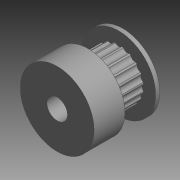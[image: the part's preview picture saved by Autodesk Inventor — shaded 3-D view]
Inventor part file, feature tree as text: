
AUTODESK INVENTOR PART (.ipt)
format: ipt  version: 2015 SP1 (Build 190203100, 203)  size: 155,648 bytes
history: native  units: mm
features: sketch x2, revolve x1, extrude x1, pattern_circular x1
ambient origin geometry x8: Origin, YZ Plane, XZ Plane, XY Plane, X Axis, Y Axis, Z Axis, Center Point
bodies: Solid1 (feature_tree)
feature tree (5):
  revolve  "Revolution1"  [1 undecoded]
  extrude  "Extrusion1"  Depth=9.0mm
  pattern_circular  "Circular Pattern1"  [2 undecoded]
  sketch  "Sketch1"  dims[d0=2.5mm d1=7.5mm]
  sketch  "Sketch2"  dims[d2=7.5mm d3=9.0mm d4=1.0mm d6=6.1mm d7=90.0deg d8=2.0mm d9=6.7mm d10=10.0mm d11=0.0mm d12=200.0mm d13=360.0deg]
note: 3 required parameter values undecoded (feature->parameter linkage not recoverable at this tier; creation-order binding heuristic only, values carry confidence <= 0.55)